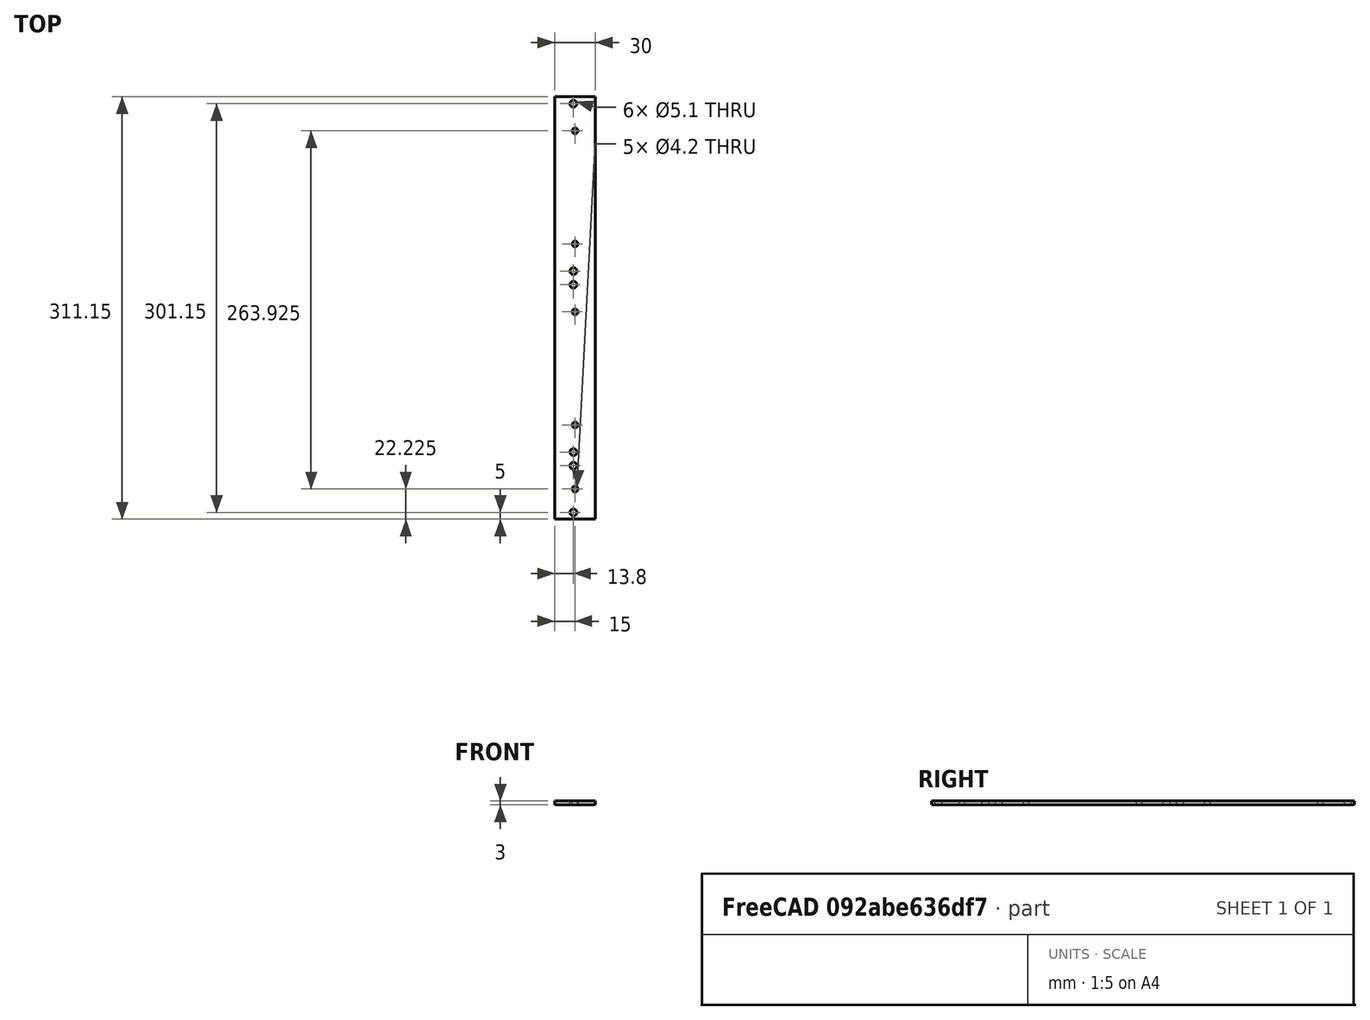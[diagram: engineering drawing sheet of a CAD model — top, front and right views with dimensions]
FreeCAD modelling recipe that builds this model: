
FCSTD DOCUMENT  (FreeCAD 0.17R13541 (Git))
Label: Sidepanel_7HE
License: All rights reserved
LicenseURL: http://en.wikipedia.org/wiki/All_rights_reserved
objects: TechDraw::DrawViewDimension×26, Sketcher::SketchObject×2, TechDraw::DrawProjGroupItem×2, PartDesign::Pad×1, PartDesign::Pocket×1, PartDesign::Body×1, TechDraw::DrawSVGTemplate×1, TechDraw::DrawProjGroup×1, TechDraw::DrawPage×1
note: 7 computed .brp shape members not serialized (recipe doc carries the construction recipe); baked Part::Feature solids carry a one-line shape summary decoded from their .brp

FEATURE [Sketcher::SketchObject] Sketch
  MapMode = 5
  Support = -> [XY_Plane]
  sketch-geometry (4):
    g0: LineSegment StartX=-30 StartY=311.15 StartZ=0 EndX=0 EndY=311.15 EndZ=0
    g1: LineSegment StartX=0 StartY=311.15 StartZ=0 EndX=0 EndY=0 EndZ=0
    g2: LineSegment StartX=0 StartY=0 StartZ=0 EndX=-30 EndY=0 EndZ=0
    g3: LineSegment StartX=-30 StartY=0 StartZ=0 EndX=-30 EndY=311.15 EndZ=0
  constraints (11):
    c: Coincident(g0,g1)
    c: Coincident(g1,g2)
    c: Coincident(g2,g3)
    c: Coincident(g3,g0)
    c: Horizontal(g0)
    c: Horizontal(g2)
    c: Vertical(g1)
    c: Vertical(g3)
    c: DistanceX(g0,g0) = 30
    c: DistanceY(g1,g1) = 311.15
    c: Coincident(g1,g-1)
FEATURE [PartDesign::Pad] Pad
  Length = 3
  Length2 = 100
  Profile = -> Sketch
  Type = 0
FEATURE [Sketcher::SketchObject] Sketch001
  ExternalGeometry = -> [Pad]
  MapMode = 5
  Placement = pos=(0,0,3) rot=(0,0,1;0rad)
  Support = -> [Pad]
  sketch-geometry (13):
    g0: LineSegment [constr] StartX=-30 StartY=44.45 StartZ=0 EndX=0 EndY=44.45 EndZ=0
    g1: LineSegment [constr] StartX=-30 StartY=177.8 StartZ=0 EndX=0 EndY=177.8 EndZ=0
    g2: Circle CenterX=-16.2 CenterY=5 CenterZ=0 NormalX=0 NormalY=0 NormalZ=1 AngleXU=0 Radius=2.55
    g3: Circle CenterX=-16.2 CenterY=39.45 CenterZ=0 NormalX=0 NormalY=0 NormalZ=1 AngleXU=0 Radius=2.55
    g4: Circle CenterX=-16.2 CenterY=49.45 CenterZ=0 NormalX=0 NormalY=0 NormalZ=1 AngleXU=0 Radius=2.55
    g5: Circle CenterX=-16.2 CenterY=172.8 CenterZ=0 NormalX=0 NormalY=0 NormalZ=1 AngleXU=0 Radius=2.55
    g6: Circle CenterX=-16.2 CenterY=182.8 CenterZ=0 NormalX=0 NormalY=0 NormalZ=1 AngleXU=0 Radius=2.55
    g7: Circle CenterX=-16.2 CenterY=306.15 CenterZ=0 NormalX=0 NormalY=0 NormalZ=1 AngleXU=0 Radius=2.55
    g8: Circle CenterX=-15 CenterY=22.225 CenterZ=0 NormalX=0 NormalY=0 NormalZ=1 AngleXU=0 Radius=2.1
    g9: Circle CenterX=-15 CenterY=69.45 CenterZ=0 NormalX=0 NormalY=0 NormalZ=1 AngleXU=0 Radius=2.1
    g10: Circle CenterX=-15 CenterY=152.8 CenterZ=0 NormalX=0 NormalY=0 NormalZ=1 AngleXU=0 Radius=2.1
    g11: Circle CenterX=-15 CenterY=202.8 CenterZ=0 NormalX=0 NormalY=0 NormalZ=1 AngleXU=0 Radius=2.1
    g12: Circle CenterX=-15 CenterY=286.15 CenterZ=0 NormalX=0 NormalY=0 NormalZ=1 AngleXU=0 Radius=2.1
  constraints (41):
    c: Horizontal(g0)
    c: Horizontal(g1)
    c: DistanceY(g-1,g0) = 44.45
    c: DistanceY(g0,g1) = 133.35
    c: Equal(g0,g-5)
    c: Equal(g1,g-5)
    c: DistanceX(g-1,g0) = 0
    c: DistanceX(g-1,g1) = 0
    c: DistanceX(g-6,g2) = 13.8
    c: DistanceX(g-6,g3) = 13.8
    c: DistanceX(g-6,g4) = 13.8
    c: DistanceX(g-6,g5) = 13.8
    c: DistanceX(g-6,g6) = 13.8
    c: DistanceX(g-6,g7) = 13.8
    c: Radius(g2) = 2.55
    c: Radius(g3) = 2.55
    c: Radius(g4) = 2.55
    c: Radius(g5) = 2.55
    c: Radius(g6) = 2.55
    c: Radius(g7) = 2.55
    c: DistanceY(g-6,g2) = 5
    c: DistanceY(g3,g0) = 5
    c: DistanceY(g0,g4) = 5
    c: DistanceY(g5,g1) = 5
    c: DistanceY(g1,g6) = 5
    c: DistanceY(g7,g-6) = 5
    c: DistanceY(g8) = 22.225
    c: DistanceX(g-6,g8) = 15
    c: Radius(g8) = 2.1
    c: DistanceY(g0,g9) = 25
    c: DistanceX(g0,g9) = 15
    c: Radius(g9) = 2.1
    c: DistanceX(g1,g10) = 15
    c: DistanceY(g10,g1) = 25
    c: Radius(g10) = 2.1
    c: DistanceY(g1,g11) = 25
    c: DistanceX(g1,g11) = 15
    c: Radius(g11) = 2.1
    c: DistanceX(g-6,g12) = 15
    c: DistanceY(g12,g-6) = 25
    c: Radius(g12) = 2.1
FEATURE [PartDesign::Pocket] Pocket
  BaseFeature = -> Pad
  Length = 5
  Length2 = 100
  Profile = -> Sketch001
  Type = 1
FEATURE [PartDesign::Body] Body
  Group = -> [Sketch,Pad,Sketch001,Pocket]
  Origin = -> Origin
  Tip = -> Pocket
FEATURE [TechDraw::DrawSVGTemplate] Template
  EditableTexts = AUTHOR_NAME=Oliver Walczak; DN=1; DRAWING_TITLE=Sidepanel 7HE; FC-DATE=27.12.2018; FC-REV=REV A; FC-SC=1; FC-SH=1 / 1; FC-SI=A4; PN=-
  Height = 297
  Orientation = 0
  Width = 210
FEATURE [TechDraw::DrawProjGroupItem] ProjItem  label="Front"
  CoarseView = false
  Direction = (0,0,1)
  Focus = 100
  HardHidden = false
  IsoCount = 0
  IsoHidden = false
  IsoVisible = false
  LockPosition = false
  Perspective = false
  Rotation = 0
  RotationVector = (1,0,0)
  ScaleType = 0
  SeamHidden = false
  SeamVisible = false
  SmoothHidden = false
  SmoothVisible = false
  Source = -> [Pocket]
  Type = 0
  X = 0
  Y = 0
FEATURE [TechDraw::DrawProjGroupItem] ProjItem001  label="Persp"
  CoarseView = false
  Direction = (-1,1,1)
  Focus = 100
  HardHidden = false
  IsoCount = 0
  IsoHidden = false
  IsoVisible = false
  LockPosition = false
  Perspective = false
  Rotation = 0
  RotationVector = (1,0,1)
  Scale = 0.5
  ScaleType = 2
  SeamHidden = false
  SeamVisible = false
  SmoothHidden = false
  SmoothVisible = false
  Source = -> [Pocket]
  Type = 6
  X = 81.4406
  Y = 1.15501
FEATURE [TechDraw::DrawProjGroup] ProjGroup
  Anchor = -> ProjItem
  AutoDistribute = false
  CubeDirs = (6) [(0,-1,1.83697e-16),(0,1.83697e-16,1),(-1,0,0),(0,-1.83697e-16,-1),(1,0,0),(0,1,-1.83697e-16)]
  CubeRotations = (6) [(1,0,0),(1,0,0),(0,-1.83697e-16,1),(-1,0,0),(0,1.83697e-16,-1),(1,0,0)]
  LockPosition = false
  ProjectionType = 0
  Rotation = 0
  Scale = 0.61
  ScaleType = 2
  Source = -> [Pocket]
  Views = -> [ProjItem,ProjItem001]
  X = 67.185
  Y = 185.335
  spacingX = 15
  spacingY = 15
FEATURE [TechDraw::DrawViewDimension] Dimension
  FormatSpec = %.2f
  LockPosition = false
  MeasureType = 1
  References2D = -> [ProjItem]
  Rotation = 0
  ScaleType = 0
  Type = 1
  X = -16.6896
  Y = -101.771
FEATURE [TechDraw::DrawViewDimension] Dimension001
  FormatSpec = %.2f
  LockPosition = false
  MeasureType = 1
  References2D = -> [ProjItem]
  Rotation = 0
  ScaleType = 0
  Type = 1
  X = -16.9684
  Y = 72.8925
FEATURE [TechDraw::DrawViewDimension] Dimension002
  FormatSpec = %.2f
  LockPosition = false
  MeasureType = 1
  References2D = -> [ProjItem]
  Rotation = 0
  ScaleType = 0
  Type = 2
  X = -35.1318
  Y = -71.9366
FEATURE [TechDraw::DrawViewDimension] Dimension006
  FormatSpec = %.2f
  LockPosition = false
  MeasureType = 1
  References2D = -> [ProjItem]
  Rotation = 0
  ScaleType = 0
  Type = 2
  X = -26.5281
  Y = 13.1446
FEATURE [TechDraw::DrawViewDimension] Dimension007
  FormatSpec = %.2f
  LockPosition = false
  MeasureType = 1
  References2D = -> [ProjItem]
  Rotation = 0
  ScaleType = 0
  Type = 2
  X = -26.5281
  Y = 51.6222
FEATURE [TechDraw::DrawViewDimension] Dimension011
  FormatSpec = %.2f
  LockPosition = false
  MeasureType = 1
  References2D = -> [ProjItem]
  Rotation = 0
  ScaleType = 0
  Type = 2
  X = 26.5281
  Y = 86.993
FEATURE [TechDraw::DrawViewDimension] Dimension012
  FormatSpec = %.2f
  LockPosition = false
  MeasureType = 1
  References2D = -> [ProjItem]
  Rotation = 0
  ScaleType = 0
  Type = 2
  X = 26.5281
  Y = 49.7103
FEATURE [TechDraw::DrawViewDimension] Dimension013
  FormatSpec = %.2f
  LockPosition = false
  MeasureType = 0
  References2D = -> [ProjItem001]
  References3D = -> [Pocket]
  Rotation = 0
  ScaleType = 0
  Type = 2
  X = -22.4652
  Y = 0
FEATURE [TechDraw::DrawViewDimension] Dimension014
  FormatSpec = %.2f
  LockPosition = false
  MeasureType = 0
  References2D = -> [ProjItem001]
  References3D = -> [Pocket]
  Rotation = 0
  ScaleType = 0
  Type = 0
  X = 3.34589
  Y = -80.3013
FEATURE [TechDraw::DrawViewDimension] Dimension015
  FormatSpec = %.2f
  LockPosition = false
  MeasureType = 1
  References2D = -> [ProjItem]
  Rotation = 0
  ScaleType = 0
  Type = 5
  X = 22.3696
  Y = -103.292
FEATURE [TechDraw::DrawViewDimension] Dimension016
  FormatSpec = %.2f
  LockPosition = false
  MeasureType = 1
  References2D = -> [ProjItem]
  Rotation = 0
  ScaleType = 0
  Type = 5
  X = 22.521
  Y = -45.3686
FEATURE [TechDraw::DrawViewDimension] Dimension017
  FormatSpec = %.2f
  LockPosition = false
  MeasureType = 1
  References2D = -> [ProjItem]
  Rotation = 0
  ScaleType = 0
  Type = 5
  X = 23.3893
  Y = -54.2034
FEATURE [TechDraw::DrawViewDimension] Dimension018
  FormatSpec = %.2f
  LockPosition = false
  MeasureType = 1
  References2D = -> [ProjItem]
  Rotation = 0
  ScaleType = 0
  Type = 5
  X = 18.259
  Y = -78.1344
FEATURE [TechDraw::DrawViewDimension] Dimension019
  FormatSpec = %.2f
  LockPosition = false
  MeasureType = 1
  References2D = -> [ProjItem]
  Rotation = 0
  ScaleType = 0
  Type = 5
  X = 21.581
  Y = -9.95003
FEATURE [TechDraw::DrawViewDimension] Dimension020
  FormatSpec = %.2f
  LockPosition = false
  MeasureType = 1
  References2D = -> [ProjItem]
  Rotation = 0
  ScaleType = 0
  Type = 5
  X = 22.7122
  Y = -98.0026
FEATURE [TechDraw::DrawViewDimension] Dimension021
  FormatSpec = %.2f
  LockPosition = false
  MeasureType = 1
  References2D = -> [ProjItem]
  Rotation = 0
  ScaleType = 0
  Type = 5
  X = 19.5017
  Y = 3.44148
FEATURE [TechDraw::DrawViewDimension] Dimension022
  FormatSpec = %.2f
  LockPosition = false
  MeasureType = 1
  References2D = -> [ProjItem]
  Rotation = 0
  ScaleType = 0
  Type = 5
  X = 18.9282
  Y = 22.6564
FEATURE [TechDraw::DrawViewDimension] Dimension023
  FormatSpec = %.2f
  LockPosition = false
  MeasureType = 1
  References2D = -> [ProjItem]
  Rotation = 0
  ScaleType = 0
  Type = 5
  X = 18.9282
  Y = 34.4148
FEATURE [TechDraw::DrawViewDimension] Dimension024
  FormatSpec = %.2f
  LockPosition = false
  MeasureType = 1
  References2D = -> [ProjItem]
  Rotation = 0
  ScaleType = 0
  Type = 5
  X = 19.5017
  Y = 72.2711
FEATURE [TechDraw::DrawViewDimension] Dimension025
  FormatSpec = %.2f
  LockPosition = false
  MeasureType = 1
  References2D = -> [ProjItem]
  Rotation = 0
  ScaleType = 0
  Type = 5
  X = 19.2149
  Y = 84.0295
FEATURE [TechDraw::DrawViewDimension] Dimension026
  FormatSpec = %.2f
  LockPosition = false
  MeasureType = 1
  References2D = -> [ProjItem]
  Rotation = 0
  ScaleType = 0
  Type = 2
  X = -26.4883
  Y = -23.8992
FEATURE [TechDraw::DrawViewDimension] Dimension027
  FormatSpec = %.2f
  LockPosition = false
  MeasureType = 1
  References2D = -> [ProjItem]
  Rotation = 0
  ScaleType = 0
  Type = 2
  X = -26.4883
  Y = -68.7102
FEATURE [TechDraw::DrawViewDimension] Dimension028
  FormatSpec = %.2f
  LockPosition = false
  MeasureType = 1
  References2D = -> [ProjItem]
  Rotation = 0
  ScaleType = 0
  Type = 2
  X = -26.4883
  Y = -83.2488
FEATURE [TechDraw::DrawViewDimension] Dimension029
  FormatSpec = %.2f
  LockPosition = false
  MeasureType = 1
  References2D = -> [ProjItem]
  Rotation = 0
  ScaleType = 0
  Type = 2
  X = 20.9118
  Y = -88.427
FEATURE [TechDraw::DrawViewDimension] Dimension030
  FormatSpec = %.2f
  LockPosition = false
  MeasureType = 1
  References2D = -> [ProjItem]
  Rotation = 0
  ScaleType = 0
  Type = 2
  X = 30.6706
  Y = -73.49
FEATURE [TechDraw::DrawViewDimension] Dimension031
  FormatSpec = %.2f
  LockPosition = false
  MeasureType = 1
  References2D = -> [ProjItem]
  Rotation = 0
  ScaleType = 0
  Type = 2
  X = 30.6706
  Y = -23.8992
FEATURE [TechDraw::DrawPage] Page
  KeepUpdated = true
  ProjectionType = 0
  Template = -> Template
  Views = -> [ProjGroup,Dimension,Dimension001,Dimension002,Dimension006,Dimension007,Dimension011,Dimension012,Dimension013,Dimension014,Dimension015,Dimension016,Dimension017,Dimension018,Dimension019,Dimension020,Dimension021,Dimension022,Dimension023,Dimension024,Dimension025,Dimension026,Dimension027,Dimension028,Dimension029,Dimension030,Dimension031]
